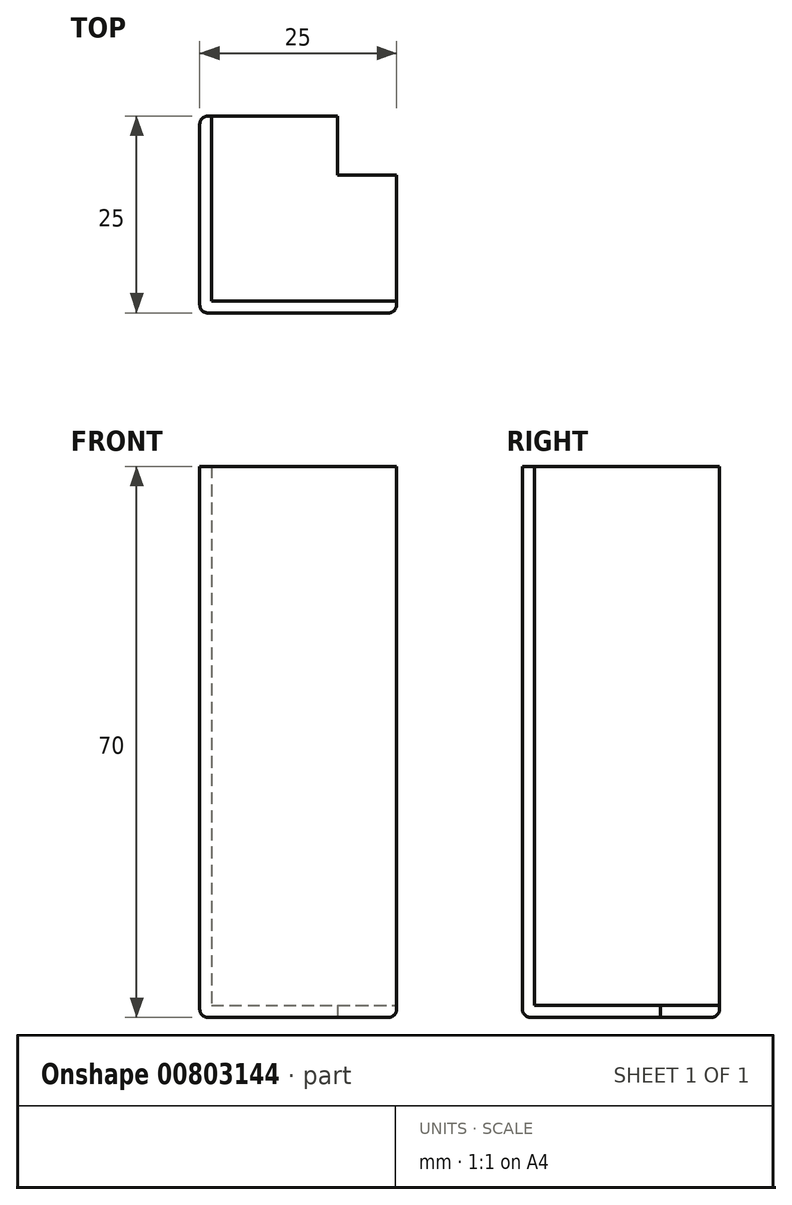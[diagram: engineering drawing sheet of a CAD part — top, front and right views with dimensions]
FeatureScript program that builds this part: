
annotation { "Feature Type Name" : "Feature", "Feature Type Description" : "" }
export const myFeature = defineFeature(function(context is Context, id is Id, definition is map)
    precondition{}
    {
        {
            var Q0;
            Q0=qCreatedBy(makeId("Top.planeOp"),FACE);
            var sketch = newSketch(context, id + "F0", { "sketchPlane" : qUnion([Q0])});
            skLineSegment(sketch, "E0", {"start": v(0, 0) * mm, "end": v(25, 0) * mm});
            skLineSegment(sketch, "E1", {"start": v(25, 0) * mm, "end": v(25, 1.5) * mm});
            skLineSegment(sketch, "E2", {"start": v(25, 1.5) * mm, "end": v(1.5, 1.5) * mm});
            skLineSegment(sketch, "E3", {"start": v(1.5, 1.5) * mm, "end": v(1.5, 25) * mm});
            skLineSegment(sketch, "E4", {"start": v(1.5, 25) * mm, "end": v(0, 25) * mm});
            skLineSegment(sketch, "E5", {"start": v(0, 25) * mm, "end": v(0, 0) * mm});
            skSolve(sketch);
        }
        {
            var Q0;
            Q0=qSketchRegion(id+"F0",true);
            extrude(context, id + "F1", {"entities" : qUnion([Q0]), "depth" : 70 * mm, "offsetDistance" : 25 * mm});
        }
        {
            var Q0;
            Q0=qCreatedBy(makeId("Front.planeOp"),FACE);
            var sketch = newSketch(context, id + "F2", { "sketchPlane" : qUnion([Q0])});
            skLineSegment(sketch, "E6", {"start": v(0, 0) * mm, "end": v(0, 25) * mm});
            skLineSegment(sketch, "E7", {"start": v(0, 25) * mm, "end": v(1.5, 25) * mm});
            skLineSegment(sketch, "E8", {"start": v(1.5, 25) * mm, "end": v(1.5, 1.5) * mm});
            skLineSegment(sketch, "E9", {"start": v(1.5, 1.5) * mm, "end": v(25, 1.5) * mm});
            skLineSegment(sketch, "E10", {"start": v(25, 1.5) * mm, "end": v(25, 0) * mm});
            skLineSegment(sketch, "E11", {"start": v(25, 0) * mm, "end": v(0, 0) * mm});
            skSolve(sketch);
        }
        {
            var Q0;
            Q0=qSketchRegion(id+"F2",true);
            extrude(context, id + "F3", {"entities" : qUnion([Q0]), "operationType" : NewBodyOperationType.ADD, "oppositeDirection" : true, "depth" : 25 * mm, "offsetDistance" : 25 * mm});
        }
        {
            var Q0;
            Q0=makeQuery(id+"F1.opExtrude","SWEPT_EDGE",EDGE,{"disambiguationData":[OSD([sQuery(id+"F0.wireOp",EDGE,"E0"),sQuery(id+"F0.wireOp",EDGE,"E5")])]});
            var Q1;
            Q1=makeQuery(id+"F1.opExtrude","CAP_EDGE",EDGE,{"disambiguationData":[OSD([sQuery(id+"F0.wireOp",EDGE,"E5")])],"isStart":true});
            var Q2;
            Q2=makeQuery(id+"F1.opExtrude","CAP_EDGE",EDGE,{"disambiguationData":[OSD([sQuery(id+"F0.wireOp",EDGE,"E0")])],"isStart":true});
            fillet(context, id + "F4", {"entities" : qUnion([Q0, Q1, Q2]), "radius" : 1 * mm, "tangentPropagation" : true, "allowEdgeOverflow" : false});
        }
        {
            var Q0;
            Q0=makeQuery(id+"F3.boolean.opBoolean","MERGE",EDGE,{"derivedFrom":[makeQuery(id+"F1.opExtrude","CAP_EDGE",EDGE,{"disambiguationData":[OSD([sQuery(id+"F0.wireOp",EDGE,"E1")])],"isStart":true}),makeQuery(id+"F3.opExtrude","SWEPT_EDGE",EDGE,{"disambiguationData":[OSD([sQuery(id+"F2.wireOp",EDGE,"E10"),sQuery(id+"F2.wireOp",EDGE,"E11")])]})]});
            var Q1;
            Q1=makeQuery(id+"F3.boolean.opBoolean","MERGE",EDGE,{"derivedFrom":[makeQuery(id+"F1.opExtrude","CAP_EDGE",EDGE,{"disambiguationData":[OSD([sQuery(id+"F0.wireOp",EDGE,"E4")])],"isStart":true}),makeQuery(id+"F3.opExtrude","CAP_EDGE",EDGE,{"disambiguationData":[OSD([sQuery(id+"F2.wireOp",EDGE,"E11")])],"isStart":false})]});
            var Q2;
            Q2=makeQuery(id+"F3.opExtrude","CAP_EDGE",EDGE,{"disambiguationData":[OSD([sQuery(id+"F2.wireOp",EDGE,"E10")])],"isStart":false});
            fillet(context, id + "F5", {"entities" : qUnion([Q0, Q1, Q2]), "radius" : 1 * mm, "tangentPropagation" : true, "allowEdgeOverflow" : false});
        }
        {
            var Q0;
            Q0=makeQuery(id+"F3.boolean.opBoolean","MERGE",FACE,{"derivedFrom":[makeQuery(id+"F1.opExtrude","CAP_FACE",FACE,{"disambiguationData":[OSD([sQuery(id+"F0.wireOp",EDGE,"E0"),sQuery(id+"F0.wireOp",EDGE,"E1"),sQuery(id+"F0.wireOp",EDGE,"E2"),sQuery(id+"F0.wireOp",EDGE,"E3"),sQuery(id+"F0.wireOp",EDGE,"E4"),sQuery(id+"F0.wireOp",EDGE,"E5")])],"isStart":true}),makeQuery(id+"F3.opExtrude","SWEPT_FACE",FACE,{"disambiguationData":[OSD([sQuery(id+"F2.wireOp",EDGE,"E11")])]})]});
            var sketch = newSketch(context, id + "F6", { "sketchPlane" : qUnion([Q0])});
            skLineSegment(sketch, "E12.bottom", {"start": v(17.5, -17.5) * mm, "end": v(42.17, -17.5) * mm});
            skLineSegment(sketch, "E12.top", {"start": v(17.5, -28.89) * mm, "end": v(42.17, -28.89) * mm});
            skLineSegment(sketch, "E12.left", {"start": v(17.5, -17.5) * mm, "end": v(17.5, -28.89) * mm});
            skLineSegment(sketch, "E12.right", {"start": v(42.17, -17.5) * mm, "end": v(42.17, -28.89) * mm});
            skSolve(sketch);
        }
        {
            var Q0;
            Q0 = qSketchRegion(id + "F6", true);
            extrude(context, id + "F7", {"entities" : qUnion([Q0]), "operationType" : NewBodyOperationType.REMOVE, "oppositeDirection" : true, "depth" : 5 * mm, "offsetDistance" : 25 * mm});
        }
    });
